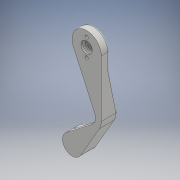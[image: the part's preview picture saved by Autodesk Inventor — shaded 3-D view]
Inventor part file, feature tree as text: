
AUTODESK INVENTOR PART (.ipt)
format: ipt  version: 2017 (Build 210142000, 142)  size: 348,160 bytes
history: native  units: mm
features: sketch x6, extrude x5, fillet x3, hole x2
ambient origin geometry x8: Origin, YZ Plane, XZ Plane, XY Plane, X Axis, Y Axis, Z Axis, Center Point
bodies: Solid1 (feature_tree)
feature tree (16):
  extrude  "Extrusion1"  Depth=9.0mm
  extrude  "Extrusion2"  Depth=5.5mm
  extrude  "Extrusion4"  Depth=23.0mm
  hole  "Hole1"  [1 undecoded]
  fillet  "Fillet1"  Radius=3.0mm
  fillet  "Fillet2"  Radius=9.0mm
  fillet  "Fillet4"  Radius=17.0mm
  extrude  "Extrusion5"  Depth=7.0mm TaperAngle=0.0deg
  hole  "Hole3"  [1 undecoded]
  extrude  "Extrusion6"  Depth=1.0mm
  sketch  "Sketch1"  dims[d0=35.0mm d2=9.0mm]
  sketch  "Sketch3"  dims[d4=9.0mm d7=5.5mm]
  sketch  "Sketch5"  dims[d8=30.0deg d9=23.0mm]
  sketch  "Sketch6"  dims[d10=6.0mm d11=3.5mm d12=3.0mm d13=0.0mm d22=9.0mm d23=17.0mm]
  sketch  "Sketch8"  dims[d25=5.0mm d29=7.0mm d30=0.0mm]
  sketch  "Sketch9"  dims[d34=5.0mm d35=60.0mm d36=25.0mm d37=20.0mm d38=0.0mm d39=18.0mm d40=11.0mm d41=5.5mm d42=5.5mm d43=2.0mm d44=6.0mm d45=4.0mm d46=2.5mm d47=90.0deg d48=8.0mm d49=20.594885mm d52=3.5mm d62=2.0mm d63=2.0mm d65=1.0mm d66=5.0mm d67=10.0mm d68=0.0mm d82=10.0mm d83=10.0mm d71=7.0mm d72=6.0mm d73=4.0mm d74=2.0mm d75=90.0deg d76=1.0mm d77=20.594885mm d80=2.5mm d81=0.0mm d78=1.0mm d79=1.0mm]
note: 2 required parameter values undecoded (feature->parameter linkage not recoverable at this tier; creation-order binding heuristic only, values carry confidence <= 0.55)
